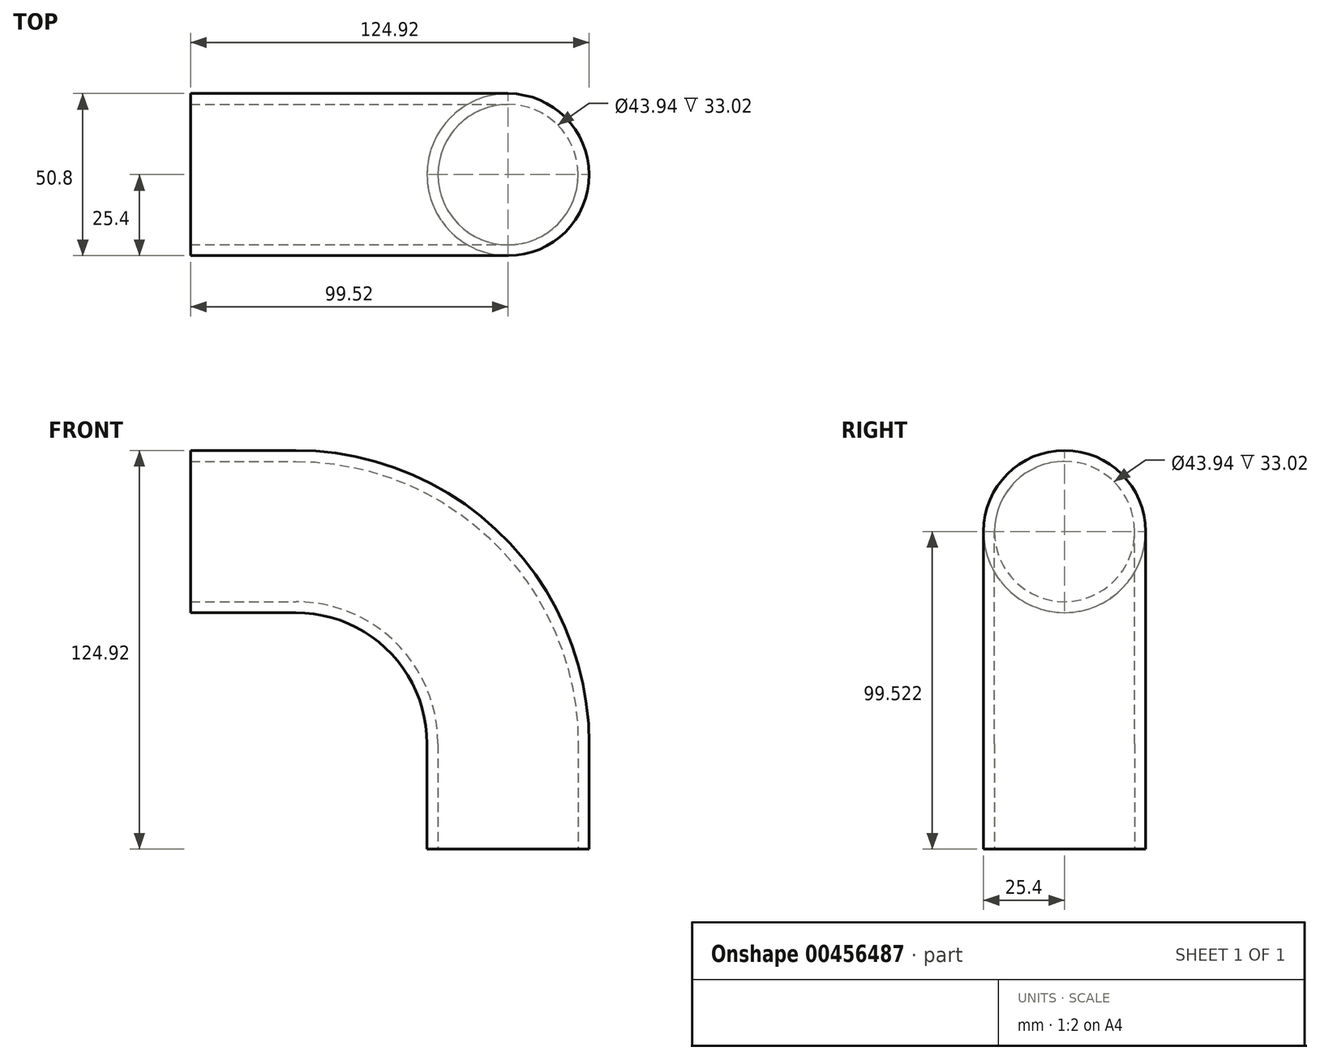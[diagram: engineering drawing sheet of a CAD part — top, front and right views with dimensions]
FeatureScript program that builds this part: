
annotation { "Feature Type Name" : "Feature", "Feature Type Description" : "" }
export const myFeature = defineFeature(function(context is Context, id is Id, definition is map)
    precondition{}
    {
        {
            var Q0;
            Q0=qCreatedBy(makeId("Top.planeOp"),FACE);
            var sketch = newSketch(context, id + "F0", { "sketchPlane" : qUnion([Q0])});
            skCircle(sketch, "E0", {"center": v(0, 0) * mm, "radius": 25.4 * mm});
            skCircle(sketch, "E1", {"center": v(0, 0) * mm, "radius": 21.97 * mm});
            skSolve(sketch);
        }
        {
            var Q0;
            Q0=qCreatedBy(makeId("Front.planeOp"),FACE);
            var sketch = newSketch(context, id + "F1", { "sketchPlane" : qUnion([Q0])});
            skArc(sketch, "E2", {"start": v(0, 0) * mm, "mid": v(-19.48, 47.02) * mm, "end": v(-66.5, 66.5) * mm});
            skLineSegment(sketch, "E3", {"start": v(-66.5, 66.5) * mm, "end": v(-66.5, -66.5) * mm, "construction": true});
            skLineSegment(sketch, "E4", {"start": v(0, 0) * mm, "end": v(-66.5, 0) * mm, "construction": true});
            skLineSegment(sketch, "E5", {"start": v(-66.5, 66.5) * mm, "end": v(-99.52, 66.5) * mm});
            skLineSegment(sketch, "E6", {"start": v(0, 0) * mm, "end": v(0, -33.02) * mm});
            skSolve(sketch);
        }
        {
            var Q0;
            Q0 = qSketchRegion(id + "F0", true);
            var Q1;
            Q1 = qConstructionFilter(qBodyType(qCreatedBy(id + "F1" ,EDGE), BodyType.WIRE), ConstructionObject.NO);
            sweep(context, id + "F2", {"profiles" : qUnion([Q0]), "path" : qUnion([Q1])});
        }
    });
